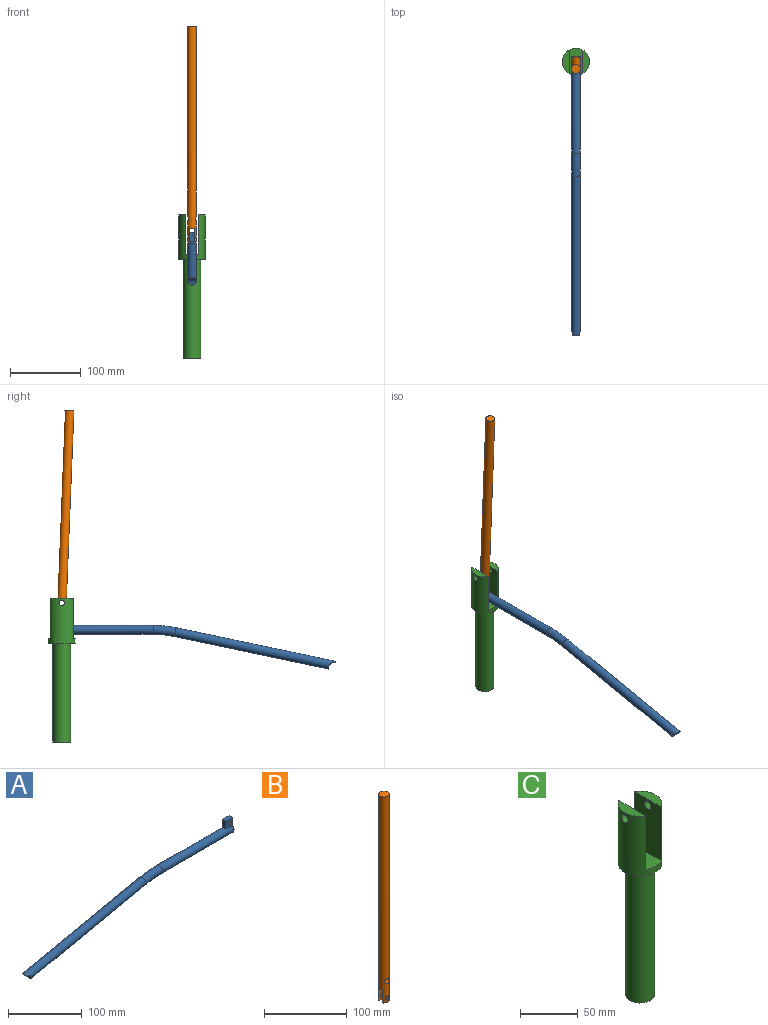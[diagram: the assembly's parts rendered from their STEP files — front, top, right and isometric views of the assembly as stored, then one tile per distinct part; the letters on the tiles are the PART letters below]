
ASSEMBLY  parts=3 mates=5
PART A: 11 faces, bbox 395x12.7x76.1 mm
  f0: plane 25.4x12.7mm, normal (1,0,0), area 209.1mm2, adj f2,f6,f9,f10
  f1: plane 8.56x1.62mm, normal (-0.98,0,-0.21), area 9.7mm2, adj f4,f5
  f2: cylinder r=6.35mm len=136.53mm, axis (-1,0,0), area 5362.9mm2, adj f0,f3,f8,f9,f10
  f3: torus R=152.4mm, axis (0,-1,0), area 1261.7mm2, adj f2,f4
  f4: cylinder r=6.35mm len=228.39mm, axis (-0.98,0,-0.21), area 8999.8mm2, adj f1,f3,f5
  f5: cylinder r=7.94mm len=12.7mm, axis (0,-1,0), area 162.3mm2, adj f1,f4
  f6: plane 12.7x6.35mm, normal (0,0,1), area 80.6mm2, adj f0,f8,f9,f10
  f7: cylinder r=3.17mm len=6.35mm, axis (0,1,0), area 126.7mm2, adj f9,f10
  f8: plane 13.55x6.35mm, normal (-1,0,0), area 82.4mm2, adj f2,f6,f9,f10
  f9: plane 13.55x12.7mm, normal (0,-1,0), area 140.4mm2, adj f0,f2,f6,f7,f8
  f10: plane 13.55x12.7mm, normal (0,1,0), area 140.4mm2, adj f0,f2,f6,f7,f8
PART B: 10 faces, bbox 12.7x12.7x304.8 mm
  f0: plane 11x3.18mm, normal (0,0,-1), area 24.8mm2, adj f4,f8
  f1: cylinder r=3.17mm len=6.35mm, axis (0,-1,0), area 55mm2, adj f4,f8
  f2: plane 11x3.18mm, normal (0,0,-1), area 24.8mm2, adj f4,f9
  f3: plane 12.7x12.7mm, normal (0,0,1), area 126.7mm2, adj f4
  f4: cylinder r=6.35mm len=304.8mm, axis (0,0,-1), area 11737.4mm2, adj f0,f1,f2,f3,f5,f6,f7,f8
  f5: cylinder r=3.97mm len=12.7mm, axis (0,-1,0), area 283mm2, adj f4
  f6: cylinder r=3.17mm len=6.35mm, axis (0,-1,0), area 55mm2, adj f4,f9
  f7: plane 12.7x6.35mm, normal (0,0,-1), area 77.1mm2, adj f4,f8,f9
  f8: plane 19.05x11mm, normal (0,-1,0), area 177.9mm2, adj f0,f1,f4,f7
  f9: plane 19.05x11mm, normal (0,1,0), area 177.9mm2, adj f2,f4,f6,f7
PART C: 11 faces, bbox 38.1x38.1x203.2 mm
  f0: plane 33x9.53mm, normal (0,0,1), area 222.9mm2, adj f1,f8
  f1: cylinder r=19.05mm len=63.5mm, axis (0,0,-1), area 5221.2mm2, adj f0,f4,f5,f6,f7,f8,f9,f10
  f2: cylinder r=12.7mm len=139.7mm, axis (0,0,-1), area 11147.6mm2, adj f3,f5
  f3: plane 25.4x25.4mm, normal (0,0,-1), area 506.7mm2, adj f2
  f4: plane 33x9.53mm, normal (0,0,1), area 222.9mm2, adj f1,f6
  f5: plane 38.1x38.1mm, normal (0,0,-1), area 633.4mm2, adj f1,f2
  f6: plane 57.15x33mm, normal (-1,0,0), area 1836.2mm2, adj f1,f4,f7,f10
  f7: plane 38.1x19.05mm, normal (0,0,1), area 694.3mm2, adj f1,f6,f8
  f8: plane 57.15x33mm, normal (1,0,0), area 1836.2mm2, adj f0,f1,f7,f9
  f9: cylinder r=3.97mm len=9.53mm, axis (1,0,0), area 232.3mm2, adj f1,f8
  f10: cylinder r=3.97mm len=9.53mm, axis (1,0,0), area 232.3mm2, adj f1,f6
PLACE A rot(axis=(0,0,1),90deg) t=(-28.03,41.09,132.04)mm
PLACE B rot(axis=(0.02,-0.02,1),90deg) t=(-28.03,34.99,138.39)mm
PLACE C t=(-28.03,33.73,-26.73)mm fixed
MATE parallel A.f6 <-> C.f1  axis (0,0,1) through (-28.03,34.74,151.09)mm
MATE cylindrical C.f9 <-> B.f5  axis (1,0,0) through (-37.55,33.73,170.12)mm
MATE planar A.f7 <-> B.f1  axis (1,0,0) through (-24.85,34.74,144.74)mm
MATE cylindrical A.f7 <-> B.f1  axis (-1,0,0) through (-28.03,34.74,144.74)mm
MATE planar C.f9 <-> B.f5  axis (1,0,0) through (-37.55,33.73,170.12)mm
